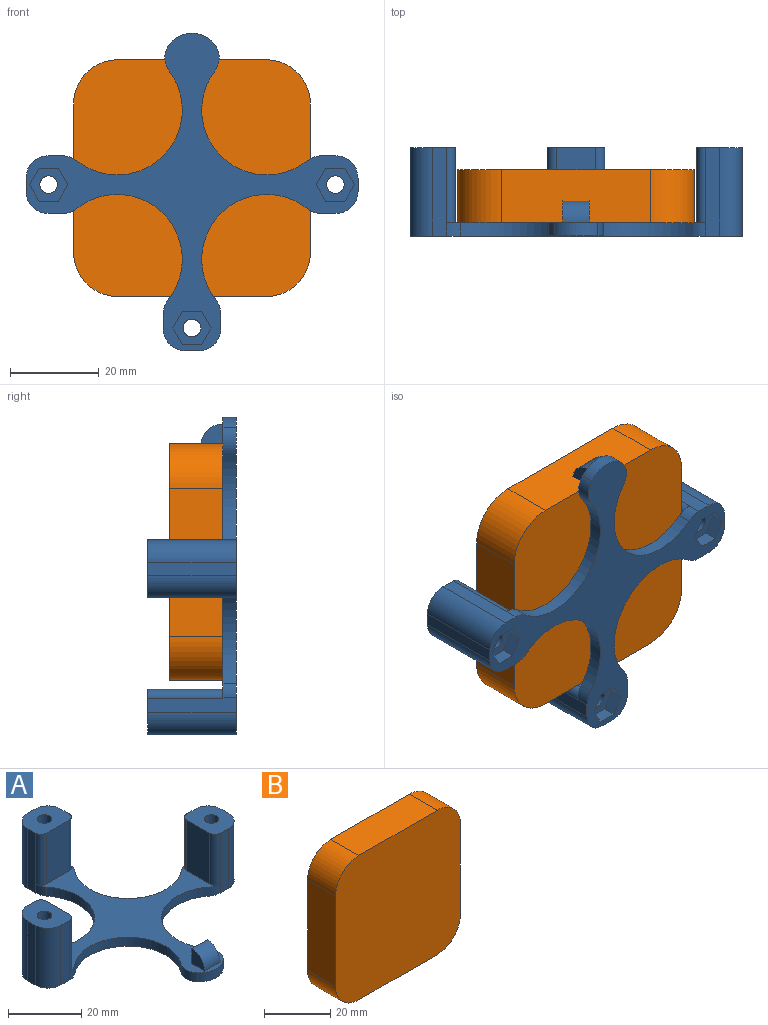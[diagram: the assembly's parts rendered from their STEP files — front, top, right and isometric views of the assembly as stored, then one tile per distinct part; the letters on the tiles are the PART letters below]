
ASSEMBLY  parts=2 mates=1
PART A: 70 faces, bbox 75x71.7x20 mm
  f0: plane 63.44x58.5mm, normal (0,0,1), area 798.9mm2, adj f8,f9,f10,f12,f13,f14,f16,f17
  f1: plane 20x3mm, normal (1,0,0), area 60mm2, adj f4,f11,f62,f63
  f2: plane 20x3mm, normal (0,1,0), area 60mm2, adj f4,f19,f58,f59
  f3: plane 20x3mm, normal (-1,0,0), area 60mm2, adj f4,f15,f60,f61
  f4: plane 75x71.69mm, normal (0,0,-1), area 1045.2mm2, adj f1,f2,f3,f8,f10,f13,f14,f17
  f5: cylinder r=2mm len=17mm, axis (0,0,1), area 213.6mm2, adj f11,f34
  f6: cylinder r=2mm len=17mm, axis (0,0,1), area 213.6mm2, adj f15,f27
  f7: cylinder r=2mm len=17mm, axis (0,0,1), area 213.6mm2, adj f19,f20
  f8: plane 20x3.35mm, normal (0,1,0), area 65.3mm2, adj f0,f4,f11,f55,f63,f67
  f9: plane 17x9mm, normal (-1,0,0), area 153mm2, adj f0,f11,f66,f67
  f10: plane 20x3.35mm, normal (0,-1,0), area 65.3mm2, adj f0,f4,f11,f53,f62,f66
  f11: plane 13x10.25mm, normal (0,0,1), area 108.2mm2, adj f1,f5,f8,f9,f10,f62,f63,f66
  f12: plane 17x9mm, normal (1,0,0), area 153mm2, adj f0,f15,f68,f69
  f13: plane 20x3.35mm, normal (0,1,0), area 65.3mm2, adj f0,f4,f15,f57,f60,f69
  f14: plane 20x3.35mm, normal (0,-1,0), area 65.3mm2, adj f0,f4,f15,f52,f61,f68
  f15: plane 13x10.25mm, normal (0,0,1), area 108.2mm2, adj f3,f6,f12,f13,f14,f60,f61,f68
  f16: plane 17x9mm, normal (0,-1,0), area 153mm2, adj f0,f19,f64,f65
  f17: plane 20x3.35mm, normal (1,0,0), area 65.3mm2, adj f0,f4,f19,f54,f59,f64
  f18: plane 20x3.35mm, normal (-1,0,0), area 65.3mm2, adj f0,f4,f19,f56,f58,f65
  f19: plane 13x10.25mm, normal (0,0,1), area 108.2mm2, adj f2,f7,f16,f17,f18,f58,f59,f64
  f20: plane 8.66x7.5mm, normal (0,0,-1), area 36.1mm2, adj f7,f21,f22,f23,f24,f25,f26
  f21: plane 3.75x3mm, normal (-0.87,0.5,0), area 13mm2, adj f4,f20,f22,f26
  f22: plane 4.33x3mm, normal (0,1,0), area 13mm2, adj f4,f20,f21,f23
  f23: plane 3.75x3mm, normal (0.87,0.5,0), area 13mm2, adj f4,f20,f22,f24
  f24: plane 3.75x3mm, normal (0.87,-0.5,0), area 13mm2, adj f4,f20,f23,f25
  f25: plane 4.33x3mm, normal (0,-1,0), area 13mm2, adj f4,f20,f24,f26
  f26: plane 3.75x3mm, normal (-0.87,-0.5,0), area 13mm2, adj f4,f20,f21,f25
  f27: plane 8.66x7.5mm, normal (0,0,-1), area 36.1mm2, adj f6,f28,f29,f30,f31,f32,f33
  f28: plane 3.75x3mm, normal (-0.87,0.5,0), area 13mm2, adj f4,f27,f29,f33
  f29: plane 4.33x3mm, normal (0,1,0), area 13mm2, adj f4,f27,f28,f30
  f30: plane 3.75x3mm, normal (0.87,0.5,0), area 13mm2, adj f4,f27,f29,f31
  f31: plane 3.75x3mm, normal (0.87,-0.5,0), area 13mm2, adj f4,f27,f30,f32
  f32: plane 4.33x3mm, normal (0,-1,0), area 13mm2, adj f4,f27,f31,f33
  f33: plane 3.75x3mm, normal (-0.87,-0.5,0), area 13mm2, adj f4,f27,f28,f32
  f34: plane 8.66x7.5mm, normal (0,0,-1), area 36.1mm2, adj f5,f35,f36,f37,f38,f39,f40
  f35: plane 3.75x3mm, normal (-0.87,0.5,0), area 13mm2, adj f4,f34,f36,f40
  f36: plane 4.33x3mm, normal (0,1,0), area 13mm2, adj f4,f34,f35,f37
  f37: plane 3.75x3mm, normal (0.87,0.5,0), area 13mm2, adj f4,f34,f36,f38
  f38: plane 3.75x3mm, normal (0.87,-0.5,0), area 13mm2, adj f4,f34,f37,f39
  f39: plane 4.33x3mm, normal (0,-1,0), area 13mm2, adj f4,f34,f38,f40
  f40: plane 3.75x3mm, normal (-0.87,-0.5,0), area 13mm2, adj f4,f34,f35,f39
  f41: cylinder r=14.67mm len=23.83mm, axis (0,0,1), area 127.1mm2, adj f0,f4,f50,f53
  f42: cylinder r=14.67mm len=23.83mm, axis (0,0,1), area 128.4mm2, adj f0,f4,f54,f55
  f43: cylinder r=14.67mm len=23.83mm, axis (0,0,1), area 128.4mm2, adj f0,f4,f56,f57
  f44: cylinder r=14.67mm len=23.83mm, axis (0,0,1), area 127.1mm2, adj f0,f4,f51,f52
  f45: cylinder r=6.5mm len=9.83mm, axis (0,0,1), area 33.4mm2, adj f0,f4,f50,f51
  f46: plane 6x5mm, normal (0,1,0), area 30mm2, adj f0,f47,f48,f49
  f47: cylinder r=5mm len=6mm, axis (-1,0,0), area 47.1mm2, adj f0,f46,f48,f49
  f48: plane 5x5mm, normal (1,0,0), area 19.6mm2, adj f0,f46,f47
  f49: plane 5x5mm, normal (-1,0,0), area 19.6mm2, adj f0,f46,f47
  f50: cylinder r=5mm len=6.27mm, axis (0,0,-1), area 20.4mm2, adj f0,f4,f41,f45
  f51: cylinder r=5mm len=6.27mm, axis (0,0,-1), area 20.4mm2, adj f0,f4,f44,f45
  f52: cylinder r=5mm len=3.12mm, axis (0,0,1), area 10.1mm2, adj f0,f4,f14,f44
  f53: cylinder r=5mm len=3.12mm, axis (0,0,1), area 10.1mm2, adj f0,f4,f10,f41
  f54: cylinder r=5mm len=3.12mm, axis (0,0,1), area 10.1mm2, adj f0,f4,f17,f42
  f55: cylinder r=5mm len=3.12mm, axis (0,0,1), area 10.1mm2, adj f0,f4,f8,f42
  f56: cylinder r=5mm len=3.12mm, axis (0,0,1), area 10.1mm2, adj f0,f4,f18,f43
  f57: cylinder r=5mm len=3.12mm, axis (0,0,1), area 10.1mm2, adj f0,f4,f13,f43
  f58: cylinder r=5mm len=20mm, axis (0,0,1), area 157.1mm2, adj f2,f4,f18,f19
  f59: cylinder r=5mm len=20mm, axis (0,0,-1), area 157.1mm2, adj f2,f4,f17,f19
  f60: cylinder r=5mm len=20mm, axis (0,0,1), area 157.1mm2, adj f3,f4,f13,f15
  f61: cylinder r=5mm len=20mm, axis (0,0,-1), area 157.1mm2, adj f3,f4,f14,f15
  f62: cylinder r=5mm len=20mm, axis (0,0,-1), area 157.1mm2, adj f1,f4,f10,f11
  f63: cylinder r=5mm len=20mm, axis (0,0,1), area 157.1mm2, adj f1,f4,f8,f11
  f64: cylinder r=2mm len=17mm, axis (0,0,1), area 53.4mm2, adj f0,f16,f17,f19
  f65: cylinder r=2mm len=17mm, axis (0,0,1), area 53.4mm2, adj f0,f16,f18,f19
  f66: cylinder r=2mm len=17mm, axis (0,0,1), area 53.4mm2, adj f0,f9,f10,f11
  f67: cylinder r=2mm len=17mm, axis (0,0,1), area 53.4mm2, adj f0,f8,f9,f11
  f68: cylinder r=2mm len=17mm, axis (0,0,-1), area 53.4mm2, adj f0,f12,f14,f15
  f69: cylinder r=2mm len=17mm, axis (0,0,-1), area 53.4mm2, adj f0,f12,f13,f15
PART B: 10 faces, bbox 53.5x12x53.5 mm
  f0: plane 33.5x12mm, normal (0,0,1), area 402mm2, adj f4,f5,f6,f9
  f1: plane 33.5x12mm, normal (-1,0,0), area 402mm2, adj f4,f5,f6,f7
  f2: plane 33.5x12mm, normal (0,0,-1), area 402mm2, adj f4,f5,f7,f8
  f3: plane 33.5x12mm, normal (1,0,0), area 402mm2, adj f4,f5,f8,f9
  f4: plane 53.5x53.5mm, normal (0,-1,0), area 2776.4mm2, adj f0,f1,f2,f3,f6,f7,f8,f9
  f5: plane 53.5x53.5mm, normal (0,1,0), area 2776.4mm2, adj f0,f1,f2,f3,f6,f7,f8,f9
  f6: cylinder r=10mm len=12mm, axis (0,-1,0), area 188.5mm2, adj f0,f1,f4,f5
  f7: cylinder r=10mm len=12mm, axis (0,1,0), area 188.5mm2, adj f1,f2,f4,f5
  f8: cylinder r=10mm len=12mm, axis (0,-1,0), area 188.5mm2, adj f2,f3,f4,f5
  f9: cylinder r=10mm len=12mm, axis (0,1,0), area 188.5mm2, adj f0,f3,f4,f5
PLACE A rot(axis=(-1,0,0),90deg) t=(0,-15,-20.38)mm
PLACE B t=(0,0,-18.91)mm
MATE fastened A.f0 <-> B.f4  axis (0,1,0) through (0,-12,-18.91)mm
